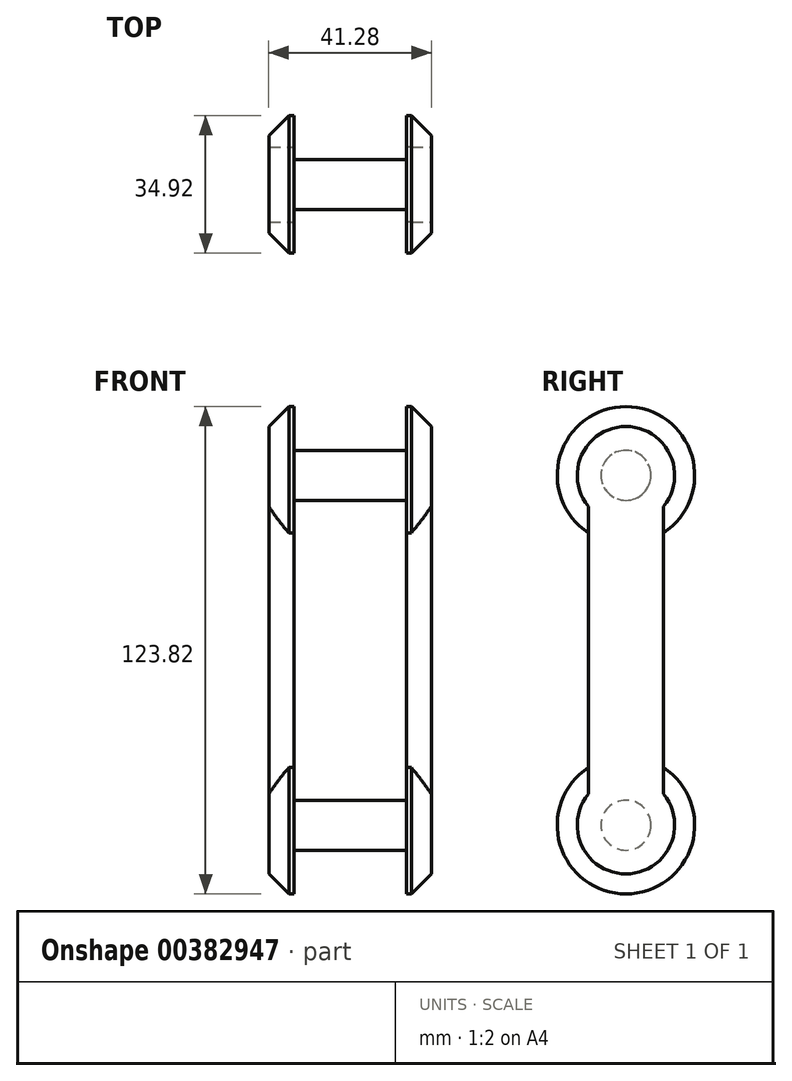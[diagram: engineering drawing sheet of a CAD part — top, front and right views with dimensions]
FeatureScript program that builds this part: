
annotation { "Feature Type Name" : "Feature", "Feature Type Description" : "" }
export const myFeature = defineFeature(function(context is Context, id is Id, definition is map)
    precondition{}
    {
        {
            var Q0;
            Q0=qCreatedBy(makeId("Right.planeOp"),FACE);
            var sketch = newSketch(context, id + "F0", { "sketchPlane" : qUnion([Q0])});
            skCircle(sketch, "E0", {"center": v(0, 0) * mm, "radius": 6.35 * mm});
            skSolve(sketch);
        }
        {
            var Q0;
            Q0 = qSketchRegion(id + "F0", true);
            extrude(context, id + "F1", {"entities" : qUnion([Q0]), "endBound" : BoundingType.SYMMETRIC, "depth" : 28.57 * mm});
        }
        {
            var Q0;
            Q0=makeQuery(id+"F1.opExtrude","CAP_FACE",FACE,{"disambiguationData":[OSD([sQuery(id+"F0.wireOp",EDGE,"E0")])],"isStart":false});
            var sketch = newSketch(context, id + "F2", { "sketchPlane" : qUnion([Q0])});
            skCircle(sketch, "E1", {"center": v(0, 0) * mm, "radius": 17.46 * mm});
            skLineSegment(sketch, "E2.bottom", {"start": v(-9.53, 0) * mm, "end": v(9.53, 0) * mm});
            skLineSegment(sketch, "E2.top", {"start": v(-9.52, 88.9) * mm, "end": v(9.52, 88.9) * mm});
            skLineSegment(sketch, "E2.left", {"start": v(-9.53, 0) * mm, "end": v(-9.53, 88.9) * mm});
            skLineSegment(sketch, "E2.right", {"start": v(9.53, 0) * mm, "end": v(9.53, 88.9) * mm});
            skCircle(sketch, "E3", {"center": v(0, 88.9) * mm, "radius": 17.46 * mm});
            skSolve(sketch);
        }
        {
            var Q0;
            {var subQ0=sQuery(id+"F2.wireOp",EDGE,"E2.top");Q0=makeQuery(id+"F2.imprint","IMPRINT",FACE,{"disambiguationData":[TD([[makeQuery(id+"F2.imprint","IMPRINT",EDGE,{"derivedFrom":subQ0}),1.0]])]});}
            var Q1;
            {var subQ0=sQuery(id+"F2.wireOp",EDGE,"E2.top");Q1=makeQuery(id+"F2.imprint","IMPRINT",FACE,{"disambiguationData":[TD([[makeQuery(id+"F2.imprint","IMPRINT",EDGE,{"derivedFrom":subQ0}),-1.0]])]});}
            var Q2;
            {var subQ0=sQuery(id+"F2.wireOp",EDGE,"E2.left");var subQ1=sQuery(id+"F2.wireOp",EDGE,"E1");var subQ2=makeQuery(id+"F2.imprint","INTERSECT",VERTEX,{"derivedFrom":[subQ1,subQ0]});Q2=makeQuery(id+"F2.imprint","IMPRINT",FACE,{"disambiguationData":[TD([[makeQuery(id+"F2.imprint","IMPRINT",EDGE,{"disambiguationData":[TD([[subQ2,1.0]])],"derivedFrom":subQ1}),-1.0]])]});}
            var Q3;
            {var subQ0=sQuery(id+"F2.wireOp",EDGE,"E2.left");var subQ3=sQuery(id+"F2.wireOp",EDGE,"E1");var subQ4=makeQuery(id+"F2.imprint","INTERSECT",VERTEX,{"derivedFrom":[subQ3,subQ0]});Q3=makeQuery(id+"F2.imprint","IMPRINT",FACE,{"disambiguationData":[TD([[makeQuery(id+"F2.imprint","IMPRINT",EDGE,{"disambiguationData":[TD([[subQ4,1.0]])],"derivedFrom":subQ3}),1.0]])]});}
            var Q4;
            {var subQ0=sQuery(id+"F2.wireOp",EDGE,"E2.bottom");var subQ1=makeQuery(id+"F1.opExtrude","CAP_EDGE",EDGE,{"disambiguationData":[OSD([sQuery(id+"F0.wireOp",EDGE,"E0")])],"isStart":false});var subQ2=makeQuery(id+"F2.imprint","INTERSECT",VERTEX,{"disambiguationData":[OD(0.0)],"derivedFrom":[subQ1,subQ0]});Q4=makeQuery(id+"F2.imprint","IMPRINT",FACE,{"disambiguationData":[TD([[makeQuery(id+"F2.imprint","IMPRINT",EDGE,{"disambiguationData":[TD([[subQ2,-1.0]])],"derivedFrom":subQ0}),-1.0]])]});}
            var Q5;
            {var subQ5=sQuery(id+"F2.wireOp",EDGE,"E2.left");var subQ8=sQuery(id+"F2.wireOp",EDGE,"E1");var subQ9=makeQuery(id+"F2.imprint","INTERSECT",VERTEX,{"derivedFrom":[subQ8,subQ5]});Q5=makeQuery(id+"F2.imprint","IMPRINT",FACE,{"disambiguationData":[TD([[makeQuery(id+"F2.imprint","IMPRINT",EDGE,{"disambiguationData":[TD([[subQ9,-1.0]])],"derivedFrom":subQ8}),1.0]])]});}
            var Q6;
            {var subQ0=sQuery(id+"F2.wireOp",EDGE,"E2.bottom");var subQ1=makeQuery(id+"F1.opExtrude","CAP_EDGE",EDGE,{"disambiguationData":[OSD([sQuery(id+"F0.wireOp",EDGE,"E0")])],"isStart":false});var subQ2=makeQuery(id+"F2.imprint","INTERSECT",VERTEX,{"disambiguationData":[OD(0.0)],"derivedFrom":[subQ1,subQ0]});Q6=makeQuery(id+"F2.imprint","IMPRINT",FACE,{"disambiguationData":[TD([[makeQuery(id+"F2.imprint","IMPRINT",EDGE,{"disambiguationData":[TD([[subQ2,-1.0]])],"derivedFrom":subQ0}),1.0]])]});}
            extrude(context, id + "F3", {"entities" : qUnion([Q0, Q1, Q2, Q3, Q4, Q5, Q6]), "operationType" : NewBodyOperationType.ADD, "depth" : 6.35 * mm});
        }
        {
            var Q0;
            Q0=makeQuery(id+"F3.opExtrude","CAP_EDGE",EDGE,{"disambiguationData":[OSD([sQuery(id+"F2.wireOp",EDGE,"E3")])],"isStart":false});
            var Q1;
            Q1=makeQuery(id+"F3.opExtrude","CAP_EDGE",EDGE,{"disambiguationData":[OSD([sQuery(id+"F2.wireOp",EDGE,"E1")])],"isStart":false});
            chamfer(context, id + "F4", {"entities" : qUnion([Q0, Q1]), "width" : 5.08 * mm, "tangentPropagation" : true});
        }
        {
            var Q0;
            Q0=makeQuery(id+"F3.opExtrude","CAP_FACE",FACE,{"disambiguationData":[OSD([sQuery(id+"F2.wireOp",EDGE,"E1"),sQuery(id+"F2.wireOp",EDGE,"E2.left"),sQuery(id+"F2.wireOp",EDGE,"E2.right"),sQuery(id+"F2.wireOp",EDGE,"E3")])],"isStart":true});
            var sketch = newSketch(context, id + "F5", { "sketchPlane" : qUnion([Q0])});
            skCircle(sketch, "E4", {"center": v(0, 88.9) * mm, "radius": 6.35 * mm});
            skSolve(sketch);
        }
        {
            var Q0;
            Q0=makeQuery(id+"F5.imprint","IMPRINT",FACE,{"disambiguationData":[TD([[makeQuery(id+"F5.imprint","IMPRINT",EDGE,{"derivedFrom":sQuery(id+"F5.wireOp",EDGE,"E4")}),1.0]])]});
            extrude(context, id + "F6", {"entities" : qUnion([Q0]), "operationType" : NewBodyOperationType.ADD, "depth" : 28.57 * mm});
        }
        {
            var Q0;
            Q0=makeQuery(id+"F1.opExtrude","SWEPT_BODY",BODY,{"disambiguationData":[OSD([sQuery(id+"F0.wireOp",EDGE,"E0")])]});
            var Q1;
            Q1=qCreatedBy(makeId("Right.planeOp"),FACE);
            mirror(context, id + "F7", {"operationType" : NewBodyOperationType.ADD, "entities" : qUnion([Q0]), "mirrorPlane" : qUnion([Q1])});
        }
    });
